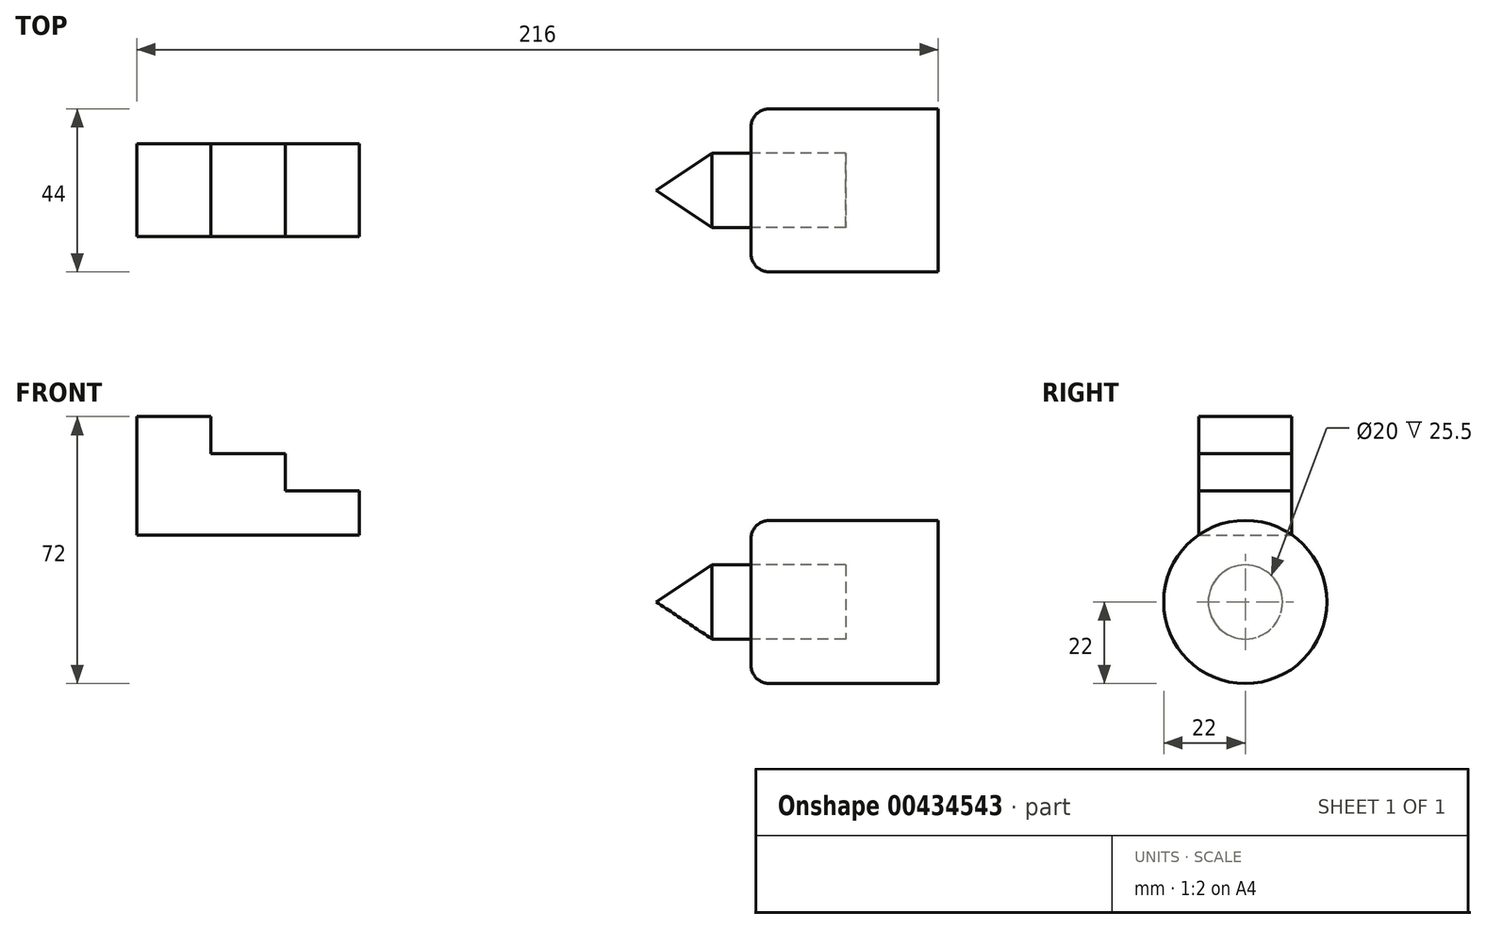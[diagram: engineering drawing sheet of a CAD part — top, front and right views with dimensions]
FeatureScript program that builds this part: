
annotation { "Feature Type Name" : "Feature", "Feature Type Description" : "" }
export const myFeature = defineFeature(function(context is Context, id is Id, definition is map)
    precondition{}
    {
        {
            var Q0;
            Q0=qCreatedBy(makeId("Front.planeOp"),FACE);
            var sketch = newSketch(context, id + "F0", { "sketchPlane" : qUnion([Q0])});
            skLineSegment(sketch, "E0.bottom", {"start": v(0, 50) * mm, "end": v(20, 50) * mm});
            skLineSegment(sketch, "E0.top", {"start": v(0, 40) * mm, "end": v(20, 40) * mm});
            skLineSegment(sketch, "E0.left", {"start": v(0, 50) * mm, "end": v(0, 40) * mm});
            skLineSegment(sketch, "E0.right", {"start": v(20, 50) * mm, "end": v(20, 40) * mm});
            skLineSegment(sketch, "E1.bottom", {"start": v(0, 40) * mm, "end": v(40, 40) * mm});
            skLineSegment(sketch, "E1.top", {"start": v(0, 30) * mm, "end": v(40, 30) * mm});
            skLineSegment(sketch, "E1.left", {"start": v(0, 40) * mm, "end": v(0, 30) * mm});
            skLineSegment(sketch, "E1.right", {"start": v(40, 40) * mm, "end": v(40, 30) * mm});
            skLineSegment(sketch, "E2.bottom", {"start": v(0, 30) * mm, "end": v(60, 30) * mm});
            skLineSegment(sketch, "E2.top", {"start": v(0, 18) * mm, "end": v(60, 18) * mm});
            skLineSegment(sketch, "E2.left", {"start": v(0, 30) * mm, "end": v(0, 18) * mm});
            skLineSegment(sketch, "E2.right", {"start": v(60, 30) * mm, "end": v(60, 18) * mm});
            skLineSegment(sketch, "E3", {"start": v(0, 0) * mm, "end": v(0, 0) * mm});
            skLineSegment(sketch, "E4.MirrorCS", {"start": v(0, -50) * mm, "end": v(0, -40) * mm});
            skLineSegment(sketch, "E5.MirrorCS", {"start": v(20, -50) * mm, "end": v(20, -40) * mm});
            skLineSegment(sketch, "E6.MirrorCS", {"start": v(0, -30) * mm, "end": v(40, -30) * mm});
            skLineSegment(sketch, "E7.MirrorCS", {"start": v(0, -40) * mm, "end": v(20, -40) * mm});
            skLineSegment(sketch, "E8.MirrorCS", {"start": v(0, -30) * mm, "end": v(0, -18) * mm});
            skLineSegment(sketch, "E9.MirrorCS", {"start": v(0, -40) * mm, "end": v(40, -40) * mm});
            skLineSegment(sketch, "E10.MirrorCS", {"start": v(0, -30) * mm, "end": v(60, -30) * mm});
            skLineSegment(sketch, "E11.MirrorCS", {"start": v(0, -18) * mm, "end": v(60, -18) * mm});
            skLineSegment(sketch, "E12.MirrorCS", {"start": v(0, -50) * mm, "end": v(20, -50) * mm});
            skLineSegment(sketch, "E13.MirrorCS", {"start": v(60, -30) * mm, "end": v(60, -18) * mm});
            skLineSegment(sketch, "E14.MirrorCS", {"start": v(0, -40) * mm, "end": v(0, -30) * mm});
            skLineSegment(sketch, "E15.MirrorCS", {"start": v(40, -40) * mm, "end": v(40, -30) * mm});
            skLineSegment(sketch, "E16", {"start": v(140, 0) * mm, "end": v(155, 10) * mm});
            skLineSegment(sketch, "E17.MirrorCS", {"start": v(140, 0) * mm, "end": v(155, -10) * mm});
            skLineSegment(sketch, "E18", {"start": v(155, 10) * mm, "end": v(155, -10) * mm});
            skLineSegment(sketch, "E19.bottom", {"start": v(155, 10) * mm, "end": v(191, 10) * mm});
            skLineSegment(sketch, "E19.top", {"start": v(155, -10) * mm, "end": v(191, -10) * mm});
            skLineSegment(sketch, "E19.right", {"start": v(191, 10) * mm, "end": v(191, -10) * mm});
            skLineSegment(sketch, "E20", {"start": v(140, 0) * mm, "end": v(191, 0) * mm});
            skLineSegment(sketch, "E21.bottom", {"start": v(165.5, 0) * mm, "end": v(191, 0) * mm});
            skLineSegment(sketch, "E21.top", {"start": v(170.5, 22) * mm, "end": v(191, 22) * mm});
            skLineSegment(sketch, "E21.left", {"start": v(165.5, 0) * mm, "end": v(165.5, 17) * mm});
            skLineSegment(sketch, "E21.right", {"start": v(191, 0) * mm, "end": v(191, 22) * mm});
            skPoint(sketch, "E22.visualSharp", {"position": v(165.5, 22) * mm});
            skArc(sketch, "E22.filletArc", {"start": v(170.5, 22) * mm, "mid": v(166.96, 20.54) * mm, "end": v(165.5, 17) * mm});
            skLineSegment(sketch, "E23.bottom", {"start": v(191, 0) * mm, "end": v(216, 0) * mm});
            skLineSegment(sketch, "E23.top", {"start": v(191, 22) * mm, "end": v(216, 22) * mm});
            skLineSegment(sketch, "E23.right", {"start": v(216, 0) * mm, "end": v(216, 22) * mm});
            skLineSegment(sketch, "E24.bottom", {"start": v(-41.93, 17.5) * mm, "end": v(-3.3, 17.5) * mm});
            skLineSegment(sketch, "E24.top", {"start": v(-41.93, -17.5) * mm, "end": v(-3.3, -17.5) * mm});
            skLineSegment(sketch, "E24.left", {"start": v(-41.93, 17.5) * mm, "end": v(-41.93, -17.5) * mm});
            skLineSegment(sketch, "E24.right", {"start": v(-3.3, 17.5) * mm, "end": v(-3.3, -17.5) * mm, "construction": true});
            skPoint(sketch, "E24.middle", {"position": v(-22.61, 0) * mm});
            skSolve(sketch);
        }
        {
            var Q0;
            Q0=makeQuery(id+"F0.imprint","IMPRINT",FACE,{"disambiguationData":[TD([[makeQuery(id+"F0.imprint","IMPRINT",EDGE,{"derivedFrom":sQuery(id+"F0.wireOp",EDGE,"E0.bottom")}),-1.0]])]});
            var Q1;
            Q1=makeQuery(id+"F0.imprint","IMPRINT",FACE,{"disambiguationData":[TD([[makeQuery(id+"F0.imprint","IMPRINT",EDGE,{"derivedFrom":sQuery(id+"F0.wireOp",EDGE,"E2.top")}),1.0]])]});
            var Q2;
            {var subQ1=sQuery(id+"F0.wireOp",EDGE,"E1.left");Q2=makeQuery(id+"F0.imprint","IMPRINT",FACE,{"disambiguationData":[TD([[makeQuery(id+"F0.imprint","IMPRINT",EDGE,{"derivedFrom":subQ1}),1.0]])]});}
            extrude(context, id + "F1", {"entities" : qUnion([Q0, Q1, Q2]), "endBound" : BoundingType.SYMMETRIC, "depth" : 25 * mm});
        }
        {
            var Q0;
            {var subQ5=sQuery(id+"F0.wireOp",EDGE,"E21.bottom");Q0=makeQuery(id+"F0.imprint","IMPRINT",FACE,{"disambiguationData":[TD([[makeQuery(id+"F0.imprint","IMPRINT",EDGE,{"derivedFrom":subQ5}),1.0]])]});}
            var Q1;
            {var subQ1=sQuery(id+"F0.wireOp",EDGE,"E19.bottom");var subQ3=sQuery(id+"F0.wireOp",EDGE,"E21.left");var subQ4=makeQuery(id+"F0.imprint","INTERSECT",VERTEX,{"derivedFrom":[subQ1,subQ3]});Q1=makeQuery(id+"F0.imprint","IMPRINT",FACE,{"disambiguationData":[TD([[makeQuery(id+"F0.imprint","IMPRINT",EDGE,{"disambiguationData":[TD([[subQ4,1.0]])],"derivedFrom":subQ1}),-1.0]])]});}
            var Q2;
            {var subQ0=sQuery(id+"F0.wireOp",EDGE,"E16");Q2=makeQuery(id+"F0.imprint","IMPRINT",FACE,{"disambiguationData":[TD([[makeQuery(id+"F0.imprint","IMPRINT",EDGE,{"derivedFrom":subQ0}),-1.0]])]});}
            var Q3;
            {var subQ5=sQuery(id+"F0.wireOp",EDGE,"E21.top");Q3=makeQuery(id+"F0.imprint","IMPRINT",FACE,{"disambiguationData":[TD([[makeQuery(id+"F0.imprint","IMPRINT",EDGE,{"derivedFrom":subQ5}),-1.0]])]});}
            var Q4;
            {var subQ3=sQuery(id+"F0.wireOp",EDGE,"E23.bottom");Q4=makeQuery(id+"F0.imprint","IMPRINT",FACE,{"disambiguationData":[TD([[makeQuery(id+"F0.imprint","IMPRINT",EDGE,{"derivedFrom":subQ3}),1.0]])]});}
            var Q5;
            Q5=sQuery(id+"F0.wireOp",EDGE,"E21.bottom");
            revolve(context, id + "F2", {"entities" : qUnion([Q0, Q1, Q2, Q3, Q4]), "axis" : qUnion([Q5]), "revolveType" : RevolveType.FULL});
        }
    });
